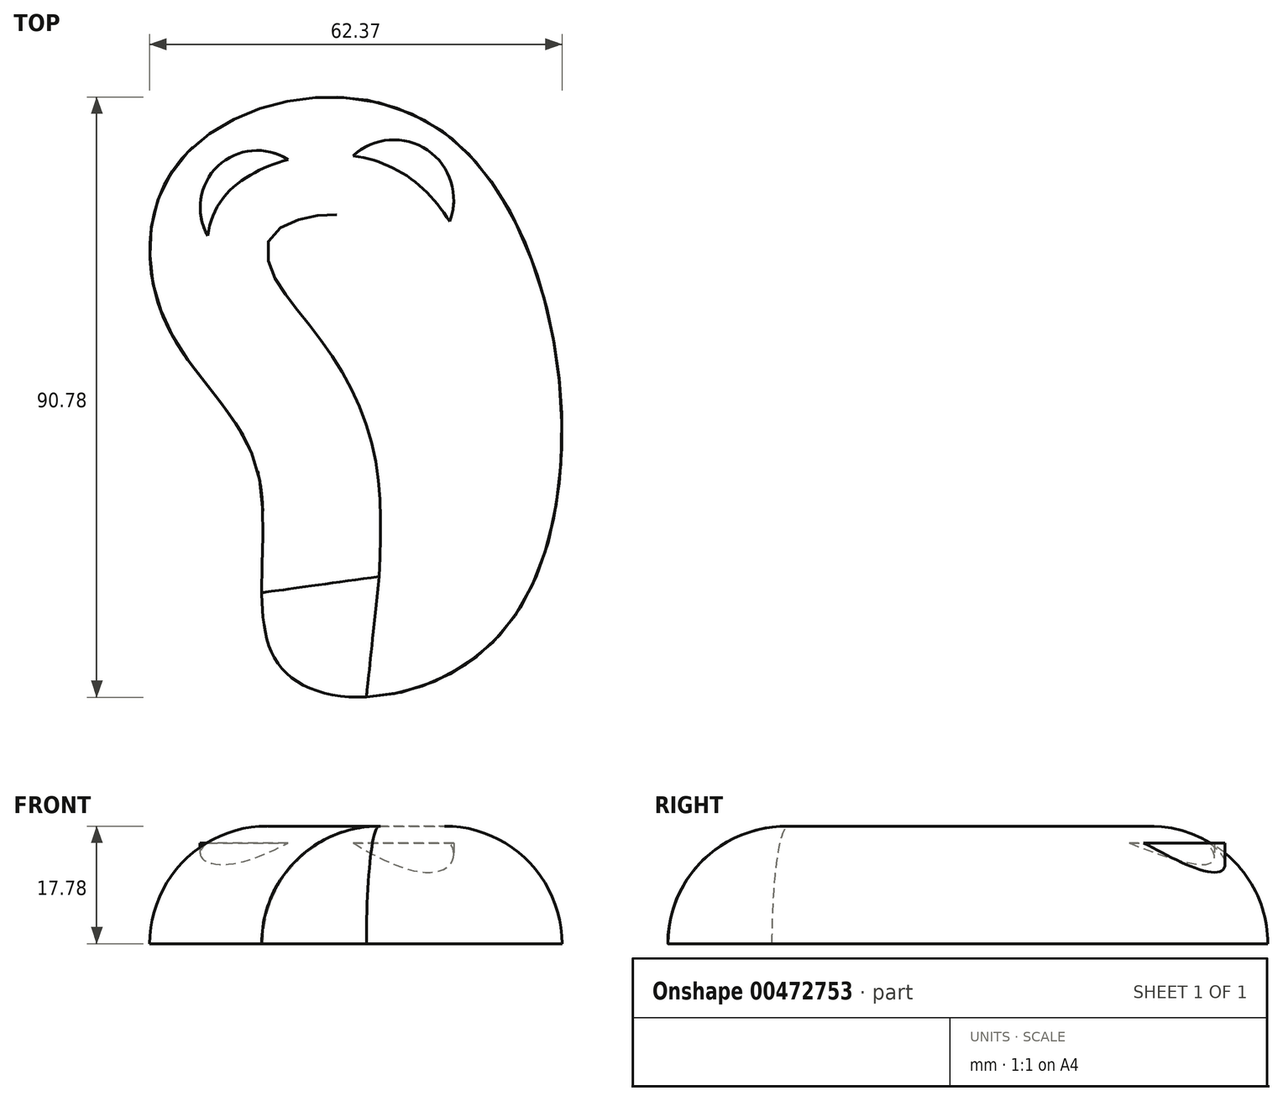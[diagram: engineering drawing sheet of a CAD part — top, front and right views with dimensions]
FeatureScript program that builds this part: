
annotation { "Feature Type Name" : "Feature", "Feature Type Description" : "" }
export const myFeature = defineFeature(function(context is Context, id is Id, definition is map)
    precondition{}
    {
        {
            var Q0;
            Q0=qCreatedBy(makeId("Top.planeOp"),FACE);
            var sketch = newSketch(context, id + "F0", { "sketchPlane" : qUnion([Q0])});
            skFitSpline(sketch, "E0", {"points": [v(-27.21, 1.86) * mm, v(-24.42, 28.14) * mm, v(16.28, 30) * mm, v(24.42, -43.03) * mm, v(-9.77, -50) * mm, v(-13.5, -20.47) * mm, v(-27.21, 1.86) * mm]});
            skSolve(sketch);
        }
        {
            var Q0;
            Q0 = qSketchRegion(id + "F0", true);
            extrude(context, id + "F1", {"entities" : qUnion([Q0]), "depth" : 17.78 * mm});
        }
        {
            var Q0;
            Q0=makeQuery(id+"F1.opExtrude","CAP_EDGE",EDGE,{"disambiguationData":[OSD([sQuery(id+"F0.wireOp",EDGE,"E0")])],"isStart":false});
            fillet(context, id + "F2", {"entities" : qUnion([Q0]), "radius" : 17.78 * mm, "tangentPropagation" : true, "allowEdgeOverflow" : false});
        }
        {
            var Q0;
            Q0=qCreatedBy(makeId("Top.planeOp"),FACE);
            var sketch = newSketch(context, id + "F3", { "sketchPlane" : qUnion([Q0])});
            skCircle(sketch, "E1", {"center": v(-13.72, 20) * mm, "radius": 8.6 * mm});
            skCircle(sketch, "E2", {"center": v(6.98, 21.17) * mm, "radius": 9.06 * mm});
            skSolve(sketch);
        }
        {
            var Q0;
            Q0 = qSketchRegion(id + "F3", true);
            extrude(context, id + "F4", {"entities" : qUnion([Q0]), "operationType" : NewBodyOperationType.ADD, "depth" : 15.24 * mm});
        }
    });
